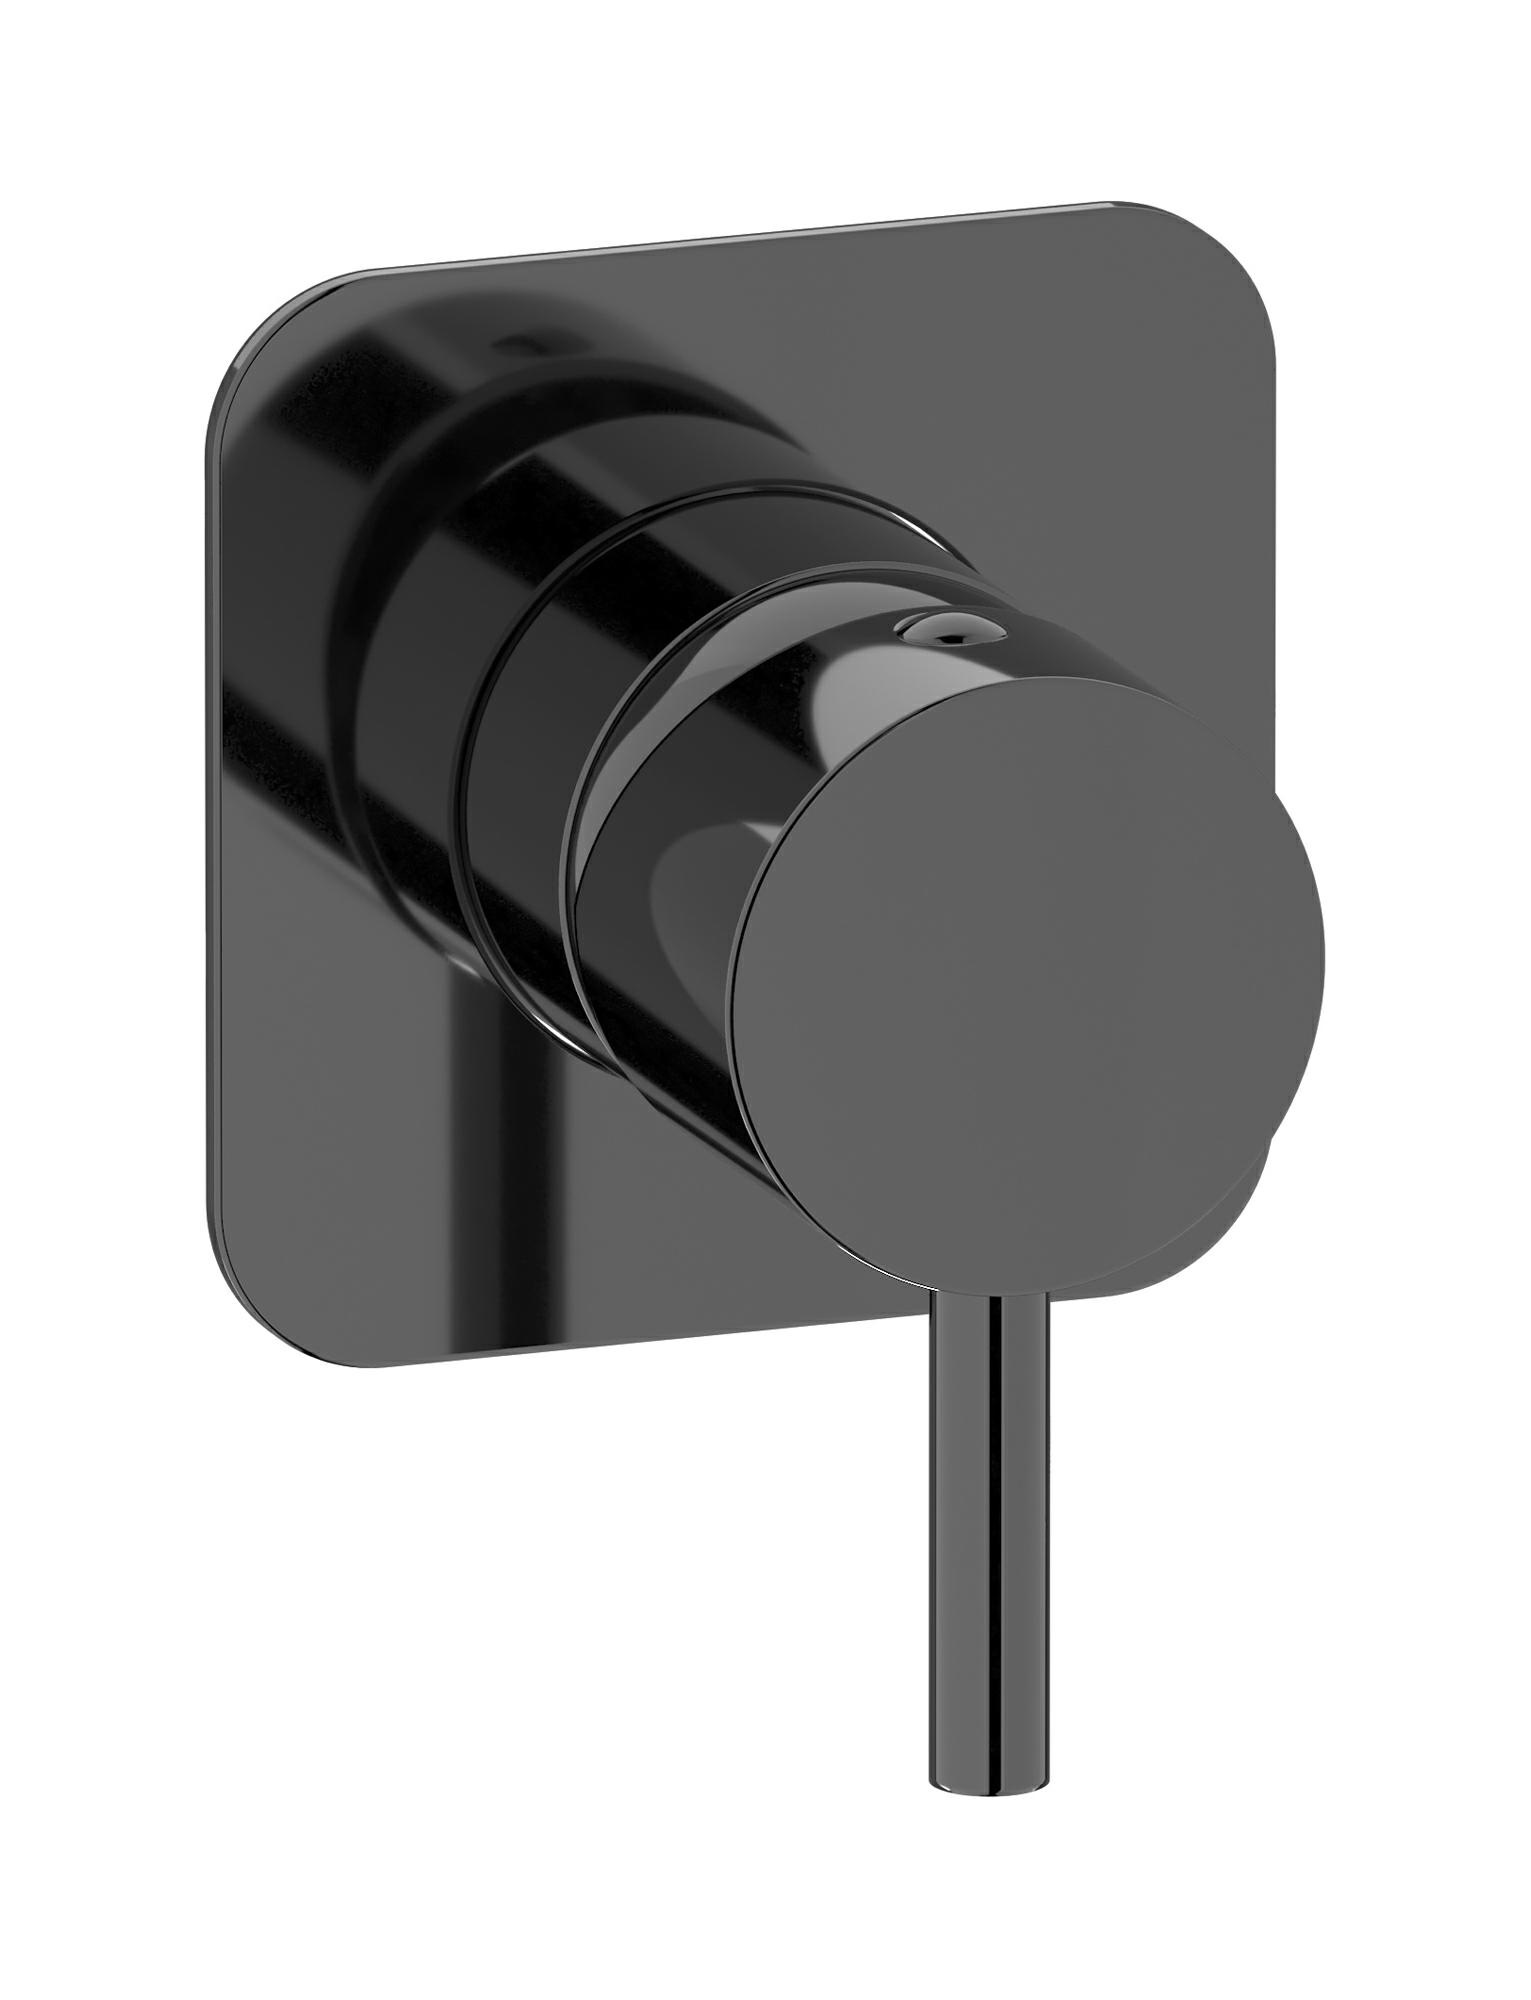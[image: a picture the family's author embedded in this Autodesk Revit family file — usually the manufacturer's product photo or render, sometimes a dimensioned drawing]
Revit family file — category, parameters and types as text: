
# Revit family: MT300
name_source: partatom
category: Apparecchi idraulici
units: mm (PartAtom-declared; Revit-internal decimal feet)

## family parameters
Basato su piano di lavoro = No
Condiviso = No
Mantieni orientamento annotazione = No
Numero OmniClass = 23.45.55.17
Punto di calcolo locali = No
Quota connettore circolare = Usa diametro
Sempre verticale = Sì
Taglio con vuoti quando caricato = No
Tipo di parte = Normale
Titolo OmniClass = Mixing Faucets

## types (13) — shared parameters
Cold water inlet = 10 mm  [stored 0.0328084 ft]
Commenti sul tipo = Wall mixer
Connessione CW = No
Connessione HW = No
Connessione di scarico = No
Connessione di ventilazione = No
Descrizione = Exposed parts for manual wall mixer
Hot water inlet = 10 mm  [stored 0.0328084 ft]
Produttore = IB Rubinetterie S.p.A.
URL = https://www.weareib.it
zero-valued in all types: Prospetto di default

## per-type parameters (varying)
| type | Finishes surface | Immagine tipo | Modello |
| Chrome | IB_Chrome | MT300CC.jpg | MT300CC |
| Brushed nickel | IB_Brushed nickel | MT300SS.jpg | MT300SS |
| Matt black | IB_matt black | MT300NP.jpg | MT300NP |
| Matt white | IB_matt white | MT300BO.jpg | MT300BO |
| Natural brass | IB_Brass | MT300ON.jpg | MT300ON |
| Black chrome | IB_Black chrome | MT300CF.jpg | MT300CF |
| Brushed black chrome | IB_Brushed black chrome | MT300CS.jpg | MT300CS |
| Pale gold | IB_Pale gold | MT300II.jpg | MT300II |
| Brushed pale gold | IB_brushed pale gold | MT300IS.jpg | MT300IS |
| Rose gold | IB_Rose gold | MT300RS.jpg | MT300RS |
| Brushed rose gold | IB_Brushed rose gold | MT300SR.jpg | MT300SR |
| Gold | IB_gold | MT300OO.jpg | MT300OO |
| Brushed gold | IB_brushed gold | MT300OS.jpg | MT300OS |

note: [stored X ft] marks values corroborated as IEEE doubles in the binary element streams (Revit-internal decimal feet)
